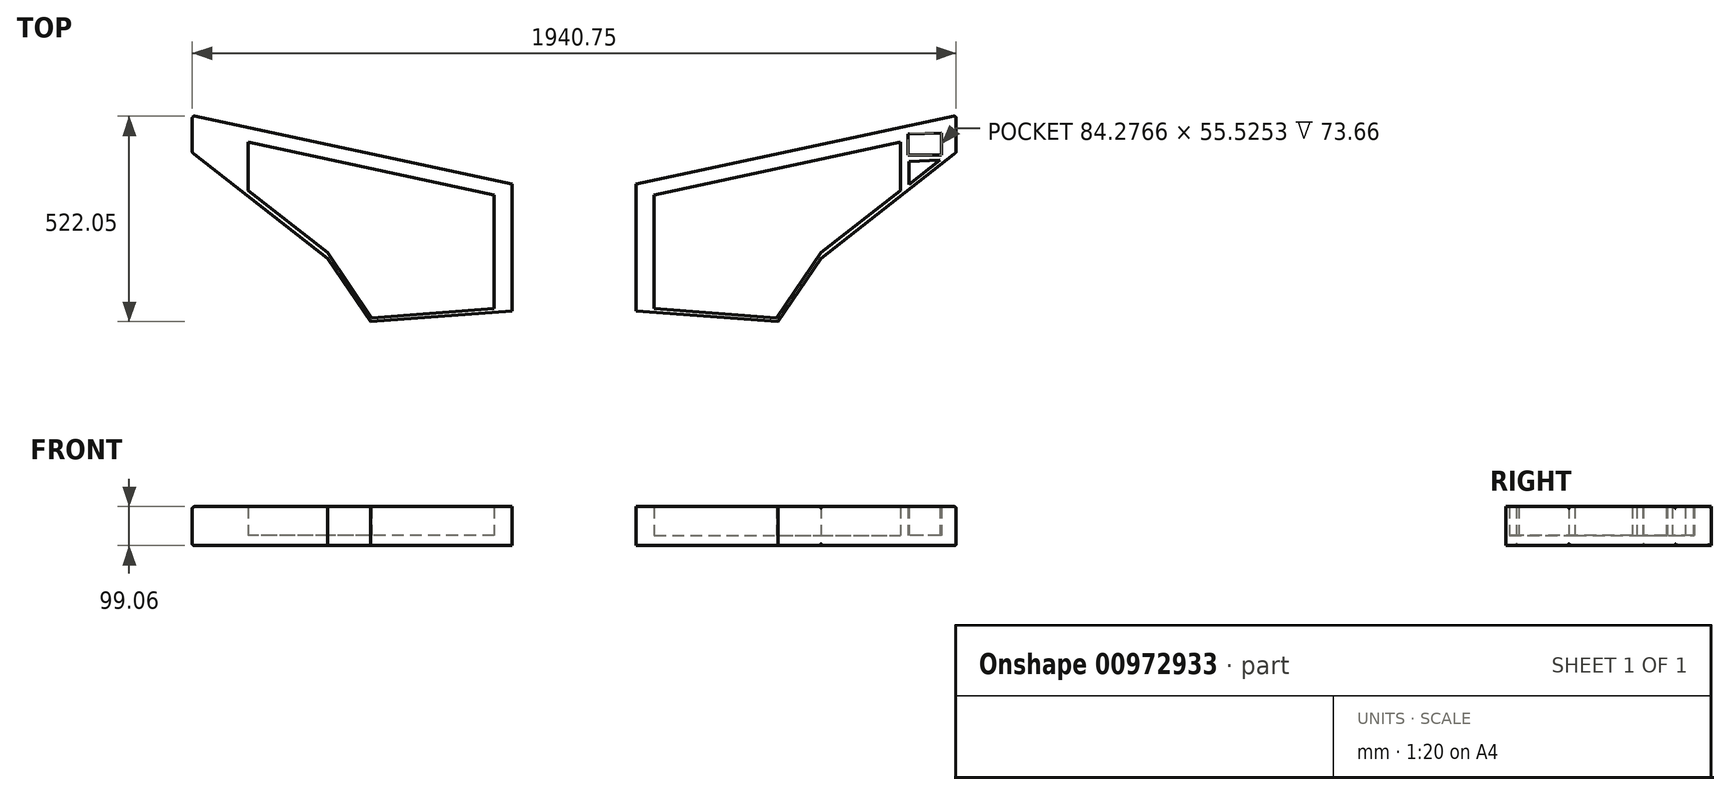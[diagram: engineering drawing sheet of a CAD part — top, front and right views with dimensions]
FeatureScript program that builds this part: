
annotation { "Feature Type Name" : "Feature", "Feature Type Description" : "" }
export const myFeature = defineFeature(function(context is Context, id is Id, definition is map)
    precondition{}
    {
        {
            var Q0;
            Q0=qCreatedBy(makeId("Top.planeOp"),FACE);
            var sketch = newSketch(context, id + "F0", { "sketchPlane" : qUnion([Q0])});
            skLineSegment(sketch, "E0", {"start": v(-33.17, -331.2) * mm, "end": v(327.1, -358.67) * mm});
            skLineSegment(sketch, "E1", {"start": v(327.1, -358.67) * mm, "end": v(436.18, -197.65) * mm});
            skLineSegment(sketch, "E2", {"start": v(-33.17, -8.61) * mm, "end": v(779.63, 164.57) * mm});
            skLineSegment(sketch, "E3", {"start": v(12.47, -325.65) * mm, "end": v(323.55, -349.37) * mm});
            skLineSegment(sketch, "E4", {"start": v(323.55, -349.37) * mm, "end": v(436.18, -183.1) * mm});
            skLineSegment(sketch, "E5", {"start": v(12.47, -36.85) * mm, "end": v(12.47, -325.65) * mm});
            skLineSegment(sketch, "E6", {"start": v(779.63, 164.57) * mm, "end": v(779.63, 71.3) * mm});
            skLineSegment(sketch, "E7", {"start": v(779.63, 71.3) * mm, "end": v(436.18, -197.65) * mm});
            skLineSegment(sketch, "E8", {"start": v(436.18, -183.1) * mm, "end": v(638.17, -24.93) * mm});
            skLineSegment(sketch, "E9", {"start": v(638.17, -24.93) * mm, "end": v(638.17, 97.86) * mm});
            skLineSegment(sketch, "E10", {"start": v(12.47, -36.85) * mm, "end": v(638.17, 97.86) * mm});
            skLineSegment(sketch, "E11", {"start": v(-33.17, -8.61) * mm, "end": v(-33.17, -331.2) * mm});
            skLineSegment(sketch, "E12", {"start": v(-190.74, 0) * mm, "end": v(-190.74, -331.2) * mm});
            skLineSegment(sketch, "E13.MirrorCS", {"start": v(-348.32, -8.61) * mm, "end": v(-348.32, -331.2) * mm});
            skLineSegment(sketch, "E14.MirrorCS", {"start": v(-393.96, -36.85) * mm, "end": v(-393.96, -325.65) * mm});
            skLineSegment(sketch, "E15.MirrorCS", {"start": v(-348.32, -8.61) * mm, "end": v(-1161.12, 164.57) * mm});
            skLineSegment(sketch, "E16.MirrorCS", {"start": v(-393.96, -36.85) * mm, "end": v(-1019.66, 97.86) * mm});
            skLineSegment(sketch, "E17.MirrorCS", {"start": v(-1019.66, -24.93) * mm, "end": v(-1019.66, 97.86) * mm});
            skLineSegment(sketch, "E18.MirrorCS", {"start": v(-1161.12, 71.3) * mm, "end": v(-817.67, -197.65) * mm});
            skLineSegment(sketch, "E19.MirrorCS", {"start": v(-817.67, -183.1) * mm, "end": v(-1019.66, -24.93) * mm});
            skLineSegment(sketch, "E20.MirrorCS", {"start": v(-705.03, -349.37) * mm, "end": v(-817.67, -183.1) * mm});
            skLineSegment(sketch, "E21.MirrorCS", {"start": v(-708.59, -358.67) * mm, "end": v(-817.67, -197.65) * mm});
            skLineSegment(sketch, "E22.MirrorCS", {"start": v(-393.96, -325.65) * mm, "end": v(-705.03, -349.37) * mm});
            skLineSegment(sketch, "E23.MirrorCS", {"start": v(-348.32, -331.2) * mm, "end": v(-708.59, -358.67) * mm});
            skLineSegment(sketch, "E24.MirrorCS", {"start": v(-1161.12, 164.57) * mm, "end": v(-1161.12, 71.3) * mm});
            skLineSegment(sketch, "E25", {"start": v(657.78, 117.94) * mm, "end": v(657.78, 64.83) * mm});
            skPoint(sketch, "E25.startSnap0", {"position": v(779.63, 117.94) * mm});
            skLineSegment(sketch, "E26", {"start": v(657.78, 64.83) * mm, "end": v(742.05, 64.83) * mm});
            skLineSegment(sketch, "E27", {"start": v(742.05, 64.83) * mm, "end": v(742.05, 120.35) * mm});
            skLineSegment(sketch, "E28", {"start": v(742.05, 120.35) * mm, "end": v(657.78, 117.94) * mm});
            skLineSegment(sketch, "E29", {"start": v(659.23, 48.84) * mm, "end": v(659.23, -9.78) * mm});
            skLineSegment(sketch, "E30", {"start": v(659.23, -9.78) * mm, "end": v(738.47, 52.26) * mm});
            skLineSegment(sketch, "E31", {"start": v(738.47, 52.26) * mm, "end": v(659.23, 48.84) * mm});
            skSolve(sketch);
        }
        {
            var Q0;
            Q0=makeQuery(id+"F0.imprint","IMPRINT",FACE,{"disambiguationData":[TD([[makeQuery(id+"F0.imprint","IMPRINT",EDGE,{"derivedFrom":sQuery(id+"F0.wireOp",EDGE,"E0")}),1.0]])]});
            extrude(context, id + "F1", {"entities" : qUnion([Q0]), "depth" : 99.06 * mm, "offsetDistance" : 25.4 * mm});
        }
        {
            var Q0;
            Q0=makeQuery(id+"F1.opExtrude","SWEPT_FACE",FACE,{"disambiguationData":[OSD([sQuery(id+"F0.wireOp",EDGE,"250f2672-8fac-466e-86b8-877a71d109f8")])]});
            var Q1;
            Q1=makeQuery(id+"F1.opExtrude","SWEPT_FACE",FACE,{"disambiguationData":[OSD([sQuery(id+"F0.wireOp",EDGE,"E2")])]});
            var Q2;
            Q2=makeQuery(id+"F1.opExtrude","SWEPT_FACE",FACE,{"disambiguationData":[OSD([sQuery(id+"F0.wireOp",EDGE,"Cz3hp2Sm-zFA2-1CJN-NmSh-LRhw8NEffxjv")])]});
            var Q3;
            Q3=makeQuery(id+"F1.opExtrude","SWEPT_FACE",FACE,{"disambiguationData":[OSD([sQuery(id+"F0.wireOp",EDGE,"pyWujWha-dyLK-AXEc-aye6-LdU3Jd9l2jL8")])]});
            var Q4;
            Q4=makeQuery(id+"F1.opExtrude","SWEPT_FACE",FACE,{"disambiguationData":[OSD([sQuery(id+"F0.wireOp",EDGE,"E1")])]});
            var Q5;
            Q5=makeQuery(id+"F1.opExtrude","SWEPT_FACE",FACE,{"disambiguationData":[OSD([sQuery(id+"F0.wireOp",EDGE,"E0")])]});
            fillet(context, id + "F2", {"entities" : qUnion([Q0, Q1, Q2, Q3, Q4, Q5]), "radius" : 5.08 * mm, "tangentPropagation" : true, "allowEdgeOverflow" : false});
        }
        {
            var Q0;
            Q0 = qSketchRegion(id + "F0", true);
            extrude(context, id + "F3", {"entities" : qUnion([Q0]), "operationType" : NewBodyOperationType.ADD, "depth" : 99.06 * mm, "offsetDistance" : 25.4 * mm});
        }
        {
            var Q0;
            Q0=makeQuery(id+"F0.imprint","IMPRINT",FACE,{"disambiguationData":[TD([[makeQuery(id+"F0.imprint","IMPRINT",EDGE,{"derivedFrom":sQuery(id+"F0.wireOp",EDGE,"E3")}),1.0]])]});
            var Q1;
            Q1=makeQuery(id+"F0.imprint","IMPRINT",FACE,{"disambiguationData":[TD([[makeQuery(id+"F0.imprint","IMPRINT",EDGE,{"derivedFrom":sQuery(id+"F0.wireOp",EDGE,"d3bc9b54-c7fa-401f-b9fb-d82ad3bd68a00.MirrorCS")}),-1.0]])]});
            var Q2;
            Q2=makeQuery(id+"F0.imprint","IMPRINT",FACE,{"disambiguationData":[TD([[makeQuery(id+"F0.imprint","IMPRINT",EDGE,{"derivedFrom":sQuery(id+"F0.wireOp",EDGE,"E14.MirrorCS")}),-1.0]])]});
            var Q3;
            Q3=makeQuery(id+"F0.imprint","IMPRINT",FACE,{"disambiguationData":[TD([[makeQuery(id+"F0.imprint","IMPRINT",EDGE,{"derivedFrom":sQuery(id+"F0.wireOp",EDGE,"E25")}),1.0]])]});
            var Q4;
            Q4=makeQuery(id+"F0.imprint","IMPRINT",FACE,{"disambiguationData":[TD([[makeQuery(id+"F0.imprint","IMPRINT",EDGE,{"derivedFrom":sQuery(id+"F0.wireOp",EDGE,"E29")}),1.0]])]});
            extrude(context, id + "F4", {"entities" : qUnion([Q0, Q1, Q2, Q3, Q4]), "operationType" : NewBodyOperationType.ADD, "depth" : 25.4 * mm, "offsetDistance" : 25.4 * mm});
        }
        {
            var Q0;
            {var subQ0=sQuery(id+"F0.wireOp",EDGE,"E6");Q0=makeQuery(id+"F3.boolean.opBoolean","MERGE",FACE,{"derivedFrom":[makeQuery(id+"F1.opExtrude","SWEPT_FACE",FACE,{"disambiguationData":[OSD([subQ0])]}),makeQuery(id+"F3.opExtrude","SWEPT_FACE",FACE,{"disambiguationData":[OSD([subQ0])]})]});}
            var Q1;
            Q1=makeQuery(id+"F3.opExtrude","SWEPT_FACE",FACE,{"disambiguationData":[OSD([sQuery(id+"F0.wireOp",EDGE,"E24.MirrorCS")])]});
            fillet(context, id + "F5", {"entities" : qUnion([Q0, Q1]), "radius" : 5.08 * mm, "tangentPropagation" : true, "allowEdgeOverflow" : false});
        }
    });
